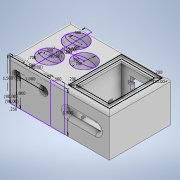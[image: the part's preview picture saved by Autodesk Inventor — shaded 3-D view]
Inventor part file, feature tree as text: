
AUTODESK INVENTOR PART (.ipt)
format: ipt  version: 2020 (Build 240168000, 168)  size: 338,944 bytes
history: native  units: in
note: dims shown in document units (in); Inventor stores cm internally (conversion verified against a paired STEP export)
features: extrude x10, sketch x7, hole x1, fillet x1
ambient origin geometry x8: Origin, YZ Plane, XZ Plane, XY Plane, X Axis, Y Axis, Z Axis, Center Point
bodies: Solid1 (feature_tree)
feature tree (19):
  extrude  "Extrusion1"  Depth=1.5in
  hole  "Hole1"  [1 undecoded]
  sketch  "Sketch2"  dims[d0=1.5in d1=1.5in]
  extrude  "Extrusion2"  TaperAngle=90.0deg  [1 undecoded]
  extrude  "Extrusion3"  Depth=2.24in TaperAngle=0.0deg
  extrude  "Extrusion4"  Depth=0.7in
  extrude  "Extrusion5"  Depth=0.39in
  extrude  "Extrusion6"  Depth=1.0in
  extrude  "Extrusion7"  TaperAngle=180.0deg  [1 undecoded]
  sketch  "Sketch7"  dims[d9=0.3125in d10=0.75in d11=0.438in d12=0.25in d13=0.5635in d14=0.5in d15=0.0in d16=0.7in]
  extrude  "Extrusion8"  Depth=0.39in
  extrude  "Extrusion9"  TaperAngle=180.0deg  [1 undecoded]
  extrude  "Extrusion10"  Depth=1.25in TaperAngle=0.0deg
  sketch  "Sketch9"  dims[d19=90.0deg d20=0.2in d21=180.0deg d22=0.39in d23=180.0deg d24=1.25in d25=0.0in d26=1.5in d27=0.0in d28=0.15in d29=0.15in d30=0.25in d31=0.0in d32=0.58in d34=1.5in d35=0.5in d36=0.4in d37=0.39in d38=0.78in d39=0.15in d40=0.125in d41=0.15in d42=0.15in d43=0.15in d44=0.15in d45=90.0deg d46=1.5in d47=0.0in d48=0.15in d49=0.0in d50=1.0in d51=0.25in d52=0.15in d53=0.0in d54=0.2in d55=135.0deg d56=0.2in d57=45.0deg d58=0.15in d59=0.0in d60=0.075in d61=0.0in d62=0.75in d63=0.45in d64=0.8in d65=0.1in d66=1.0in d67=1.0in d68=0.0in]
  fillet  "Fillet1"  Radius=1.5in
  sketch  "Sketch4"  dims[d2=0.25in d3=90.0deg]
  sketch  "Sketch5"  dims[d4=1.0in d5=90.0deg]
  sketch  "Sketch6"  dims[d6=1.0in d7=2.24in d8=0.0in]
  sketch  "Sketch8"  dims[d17=90.0deg d18=0.39in]
note: 4 required parameter values undecoded (feature->parameter linkage not recoverable at this tier; creation-order binding heuristic only, values carry confidence <= 0.55)
